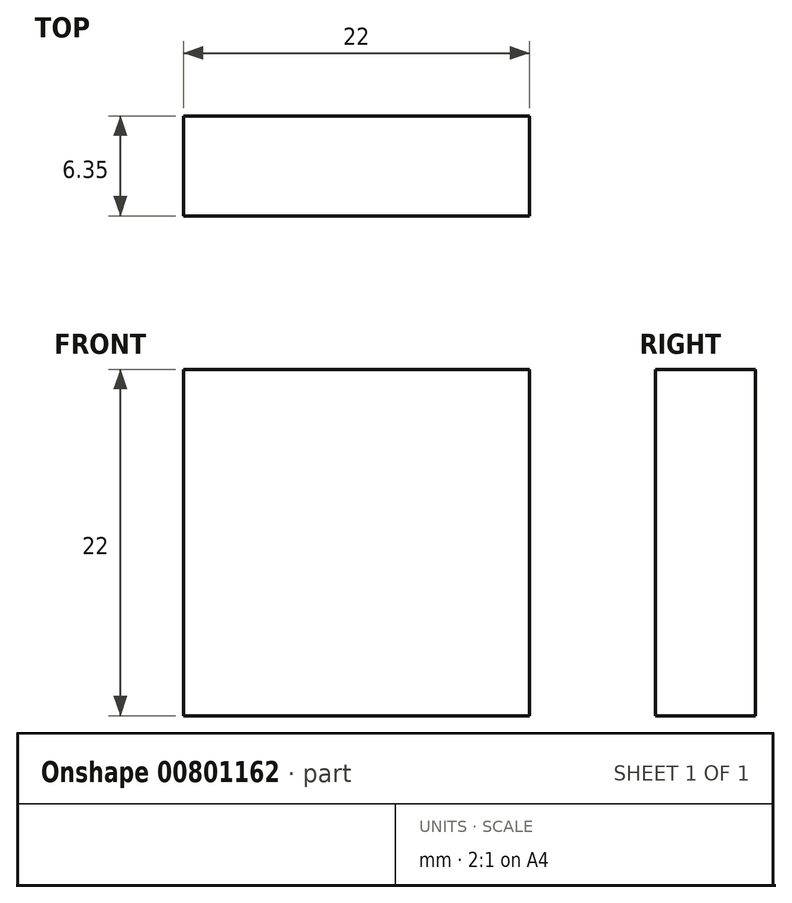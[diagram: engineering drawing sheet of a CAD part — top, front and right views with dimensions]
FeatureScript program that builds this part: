
annotation { "Feature Type Name" : "Feature", "Feature Type Description" : "" }
export const myFeature = defineFeature(function(context is Context, id is Id, definition is map)
    precondition{}
    {
        {
            var Q0;
            Q0=qCreatedBy(makeId("Front.planeOp"),FACE);
            var sketch = newSketch(context, id + "F0", { "sketchPlane" : qUnion([Q0])});
            skLineSegment(sketch, "E0.bottom", {"start": v(0, 0) * mm, "end": v(22, 0) * mm});
            skLineSegment(sketch, "E0.top", {"start": v(0, 22) * mm, "end": v(22, 22) * mm});
            skLineSegment(sketch, "E0.left", {"start": v(0, 0) * mm, "end": v(0, 22) * mm});
            skLineSegment(sketch, "E0.right", {"start": v(22, 0) * mm, "end": v(22, 22) * mm});
            skSolve(sketch);
        }
        {
            var Q0;
            Q0 = qSketchRegion(id + "F0", true);
            extrude(context, id + "F1", {"entities" : qUnion([Q0]), "depth" : 6.35 * mm, "offsetDistance" : 25.4 * mm});
        }
    });
